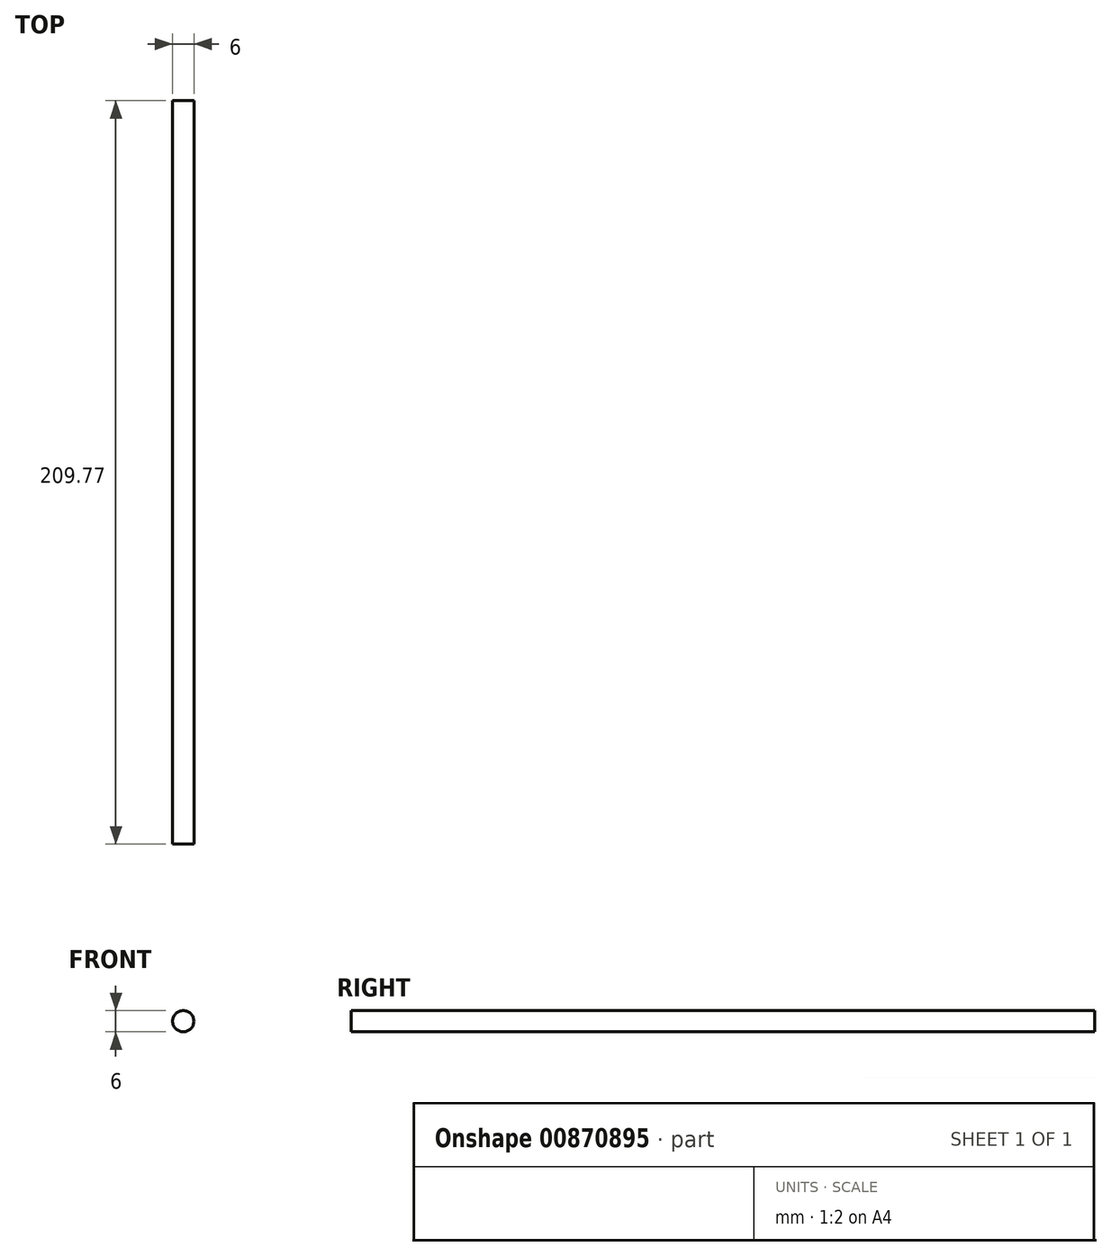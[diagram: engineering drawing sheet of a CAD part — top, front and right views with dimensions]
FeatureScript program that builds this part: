
annotation { "Feature Type Name" : "Feature", "Feature Type Description" : "" }
export const myFeature = defineFeature(function(context is Context, id is Id, definition is map)
    precondition{}
    {
        {
            var Q0;
            Q0=qCreatedBy(makeId("Front.planeOp"),FACE);
            var sketch = newSketch(context, id + "F0", { "sketchPlane" : qUnion([Q0])});
            skCircle(sketch, "E0", {"center": v(0, 0) * mm, "radius": 3 * mm});
            skSolve(sketch);
        }
        {
            var Q0;
            Q0=makeQuery(id+"F0.imprint","IMPRINT",FACE,{"disambiguationData":[TD([[makeQuery(id+"F0.imprint","IMPRINT",EDGE,{"derivedFrom":sQuery(id+"F0.wireOp",EDGE,"E0")}),1.0]])]});
            extrude(context, id + "F1", {"entities" : qUnion([Q0]), "depth" : 209.77 * mm, "offsetDistance" : 25 * mm});
        }
    });
